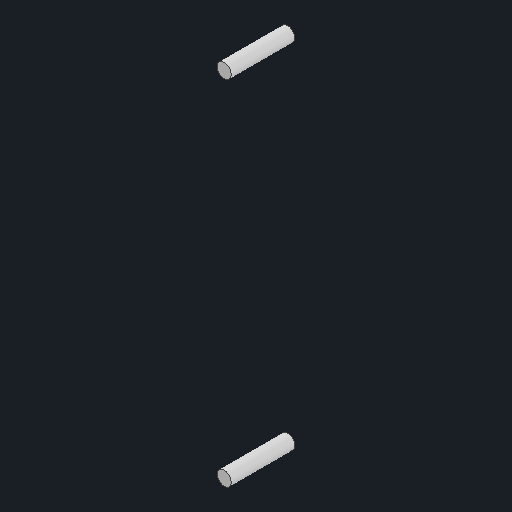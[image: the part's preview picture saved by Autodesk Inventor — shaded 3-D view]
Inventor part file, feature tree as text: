
AUTODESK INVENTOR PART (.ipt)
format: ipt  version: 2024 (Build 280153000, 153)  size: 182,272 bytes
history: native  units: mm
features: other x4, plane x1, extrude x1, sketch x1
ambient origin geometry x8: Origin, YZ Plane, XZ Plane, XY Plane, X Axis, Y Axis, Z Axis, Center Point
bodies: Body1 (feature_tree)
feature tree (7):
  other  "Sólido1"
  plane  "Plano de trabajo1"
  extrude  "Extrusión1"  Depth=18.0mm
  sketch  "Boceto1"  dims[d0=4.0mm d1=4.0mm d2=100.0mm d3=99.2mm d4=7.5mm d5=7.5mm d6=18.0mm d7=0.0mm]
  other  "<userpath>\Downloads\Piezas CMR\Marco_APM_002\Marco_apm_002-4.iam"
  other  "Marco_apm_002-4.iam"
  other  "S_horizontal:1"
